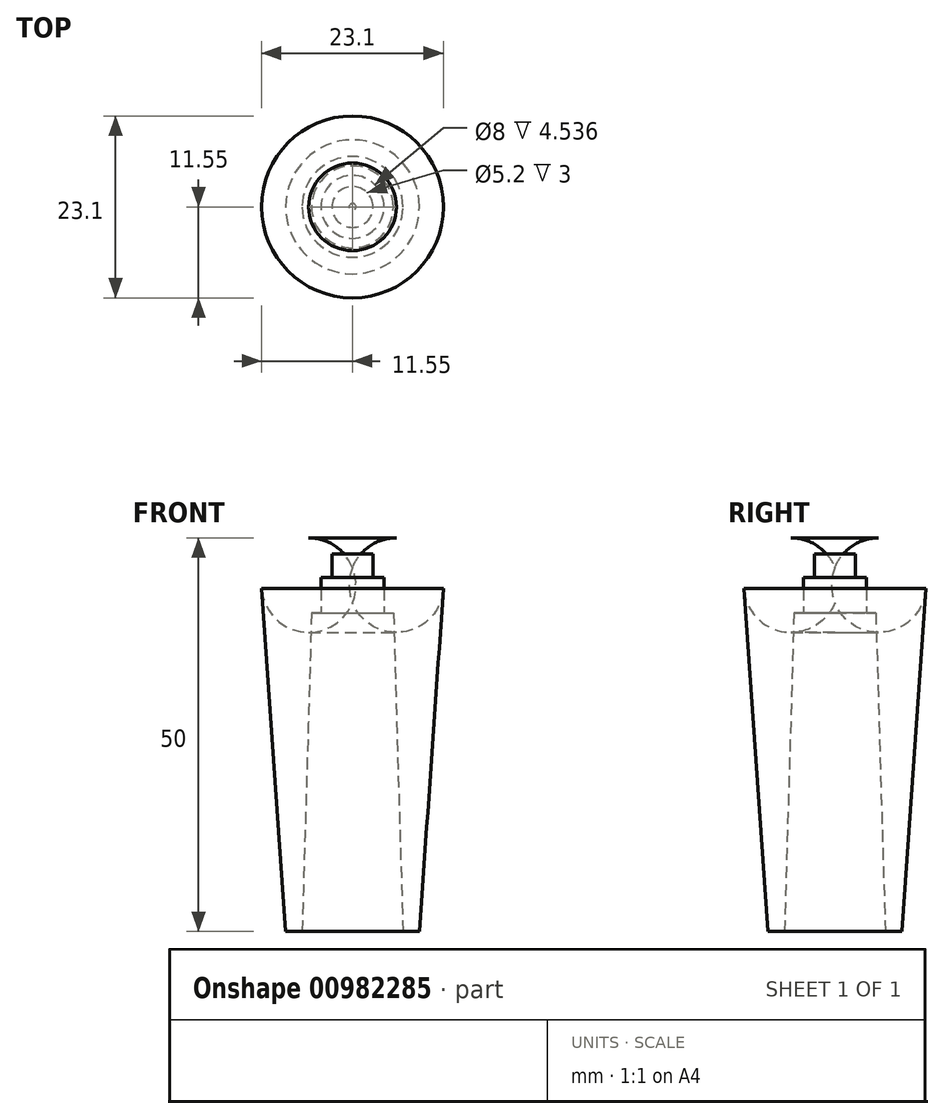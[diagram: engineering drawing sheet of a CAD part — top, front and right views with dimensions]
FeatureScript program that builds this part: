
annotation { "Feature Type Name" : "Feature", "Feature Type Description" : "" }
export const myFeature = defineFeature(function(context is Context, id is Id, definition is map)
    precondition{}
    {
        {
            var Q0;
            Q0=qCreatedBy(makeId("Front.planeOp"),FACE);
            var sketch = newSketch(context, id + "F0", { "sketchPlane" : qUnion([Q0])});
            skLineSegment(sketch, "E0", {"start": v(0, 0) * mm, "end": v(0, -50) * mm});
            skLineSegment(sketch, "E1", {"start": v(0, -50) * mm, "end": v(8.5, -50) * mm});
            skLineSegment(sketch, "E2", {"start": v(8.5, -50) * mm, "end": v(12, 0) * mm});
            skLineSegment(sketch, "E3", {"start": v(12, 0) * mm, "end": v(0, 0) * mm});
            skSolve(sketch);
        }
        {
            var Q0;
            Q0=makeQuery(id+"F0.imprint","IMPRINT",FACE,{"disambiguationData":[TD([[makeQuery(id+"F0.imprint","IMPRINT",EDGE,{"derivedFrom":sQuery(id+"F0.wireOp",EDGE,"E0")}),1.0]])]});
            var Q1;
            Q1=sQuery(id+"F0.wireOp",EDGE,"E0");
            revolve(context, id + "F1", {"surfaceOperationType" : NewSurfaceOperationType.NEW, "entities" : qUnion([Q0]), "axis" : qUnion([Q1]), "revolveType" : RevolveType.FULL});
        }
        {
            var Q0;
            Q0=qCreatedBy(makeId("Front.planeOp"),FACE);
            var sketch = newSketch(context, id + "F2", { "sketchPlane" : qUnion([Q0])});
            skLineSegment(sketch, "E4", {"start": v(0, -2.01) * mm, "end": v(0, -50.01) * mm});
            skLineSegment(sketch, "E5", {"start": v(0, -50.01) * mm, "end": v(6.4, -50.01) * mm});
            skLineSegment(sketch, "E6", {"start": v(6.4, -50.01) * mm, "end": v(5.2, -9.51) * mm});
            skLineSegment(sketch, "E7", {"start": v(5.2, -9.51) * mm, "end": v(4, -9.55) * mm});
            skLineSegment(sketch, "E8", {"start": v(4, -9.55) * mm, "end": v(4, -5.01) * mm});
            skLineSegment(sketch, "E9", {"start": v(4, -5.01) * mm, "end": v(2.6, -5.01) * mm});
            skLineSegment(sketch, "E10", {"start": v(2.6, -5.01) * mm, "end": v(2.6, -2.01) * mm});
            skLineSegment(sketch, "E11", {"start": v(2.6, -2.01) * mm, "end": v(0, -2.01) * mm});
            skSolve(sketch);
        }
        {
            var Q0;
            Q0 = qSketchRegion(id + "F2", true);
            var Q1;
            Q1=sQuery(id+"F2.wireOp",EDGE,"E4");
            revolve(context, id + "F3", {"operationType" : NewBodyOperationType.REMOVE, "surfaceOperationType" : NewSurfaceOperationType.NEW, "entities" : qUnion([Q0]), "axis" : qUnion([Q1]), "revolveType" : RevolveType.FULL, "oppositeDirection" : true});
        }
        {
            var Q0;
            Q0=makeQuery(id+"F1.opRevolve","SWEPT_EDGE",EDGE,{"disambiguationData":[OSD([sQuery(id+"F0.wireOp",EDGE,"E2"),sQuery(id+"F0.wireOp",EDGE,"E3")])]});
            fillet(context, id + "F4", {"entities" : qUnion([Q0]), "radius" : 6 * mm, "tangentPropagation" : true, "allowEdgeOverflow" : false});
        }
    });
